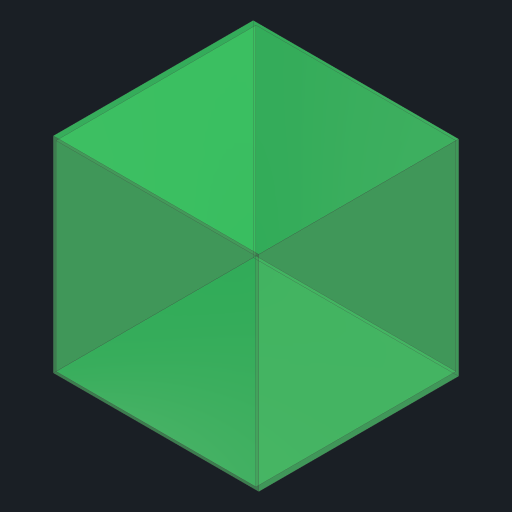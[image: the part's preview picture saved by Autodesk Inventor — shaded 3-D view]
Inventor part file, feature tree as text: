
AUTODESK INVENTOR PART (.ipt)
format: ipt  version: 2023 (Build 270158000, 158)  size: 129,536 bytes
history: native  units: in
note: dims shown in document units (in); Inventor stores cm internally (conversion verified against a paired STEP export)
features: other x3, extrude x1, shell x1, sketch x1
ambient origin geometry x8: Origin, YZ Plane, XZ Plane, XY Plane, X Axis, Y Axis, Z Axis, Center Point
bodies: Solid1 (feature_tree)
feature tree (6):
  other  "Table"
  other  "VRC High School"
  other  "VEXU Small"
  extrude  "Extrusion1"  Depth=18.5in
  shell  "Shell1"  Thickness=18.0in
  sketch  "Sketch1"  dims[d0=18.5in d1=18.5in d2=18.0in d3=0.0in d4=0.25in]
